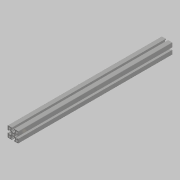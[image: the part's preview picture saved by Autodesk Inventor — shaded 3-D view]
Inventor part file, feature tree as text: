
AUTODESK INVENTOR PART (.ipt)
format: ipt  version: 2021.2 (Build 252289000, 289)  size: 201,216 bytes
history: native  units: in
note: dims shown in document units (in); Inventor stores cm internally (conversion verified against a paired STEP export)
features: other x2, extrude x1, sketch x1, projected_geometry x1
ambient origin geometry x8: Origin, YZ Plane, XZ Plane, XY Plane, X Axis, Y Axis, Z Axis, Center Point
bodies: Body1 (feature_tree)
feature tree (5):
  other  "ソリッド2"
  extrude  "押し出し1"  Depth=17.126in
  sketch  "スケッチ2"
  projected_geometry  "投影ループ1"
  other  "ソリッド1"
